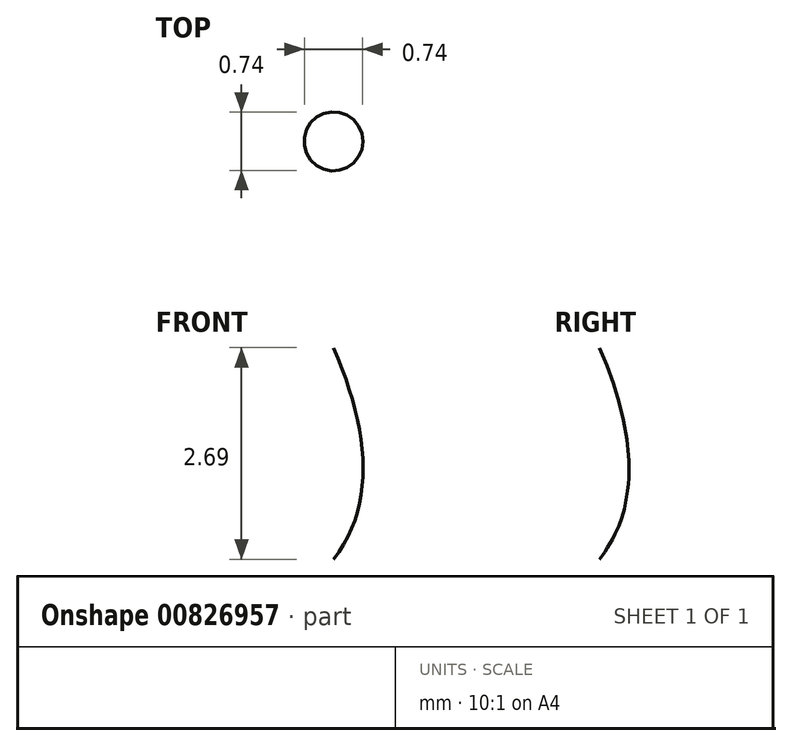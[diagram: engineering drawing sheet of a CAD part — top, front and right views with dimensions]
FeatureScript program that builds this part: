
annotation { "Feature Type Name" : "Feature", "Feature Type Description" : "" }
export const myFeature = defineFeature(function(context is Context, id is Id, definition is map)
    precondition{}
    {
        {
            var Q0;
            Q0=qCreatedBy(makeId("Front.planeOp"),FACE);
            var sketch = newSketch(context, id + "F0", { "sketchPlane" : qUnion([Q0])});
            skFitSpline(sketch, "E0", {"points": [v(0, -32.97) * mm, v(-38.8, -24.23) * mm, v(-52.04, 9.67) * mm, v(-24.5, 32.7) * mm, v(-12.31, 46.74) * mm, v(-19.2, 56.8) * mm, v(-14.43, 57.86) * mm, v(-7.55, 47.54) * mm, v(-16.55, 30.32) * mm, v(-40.39, 12.84) * mm, v(-41.45, -5.43) * mm, v(-27.94, -17.35) * mm, v(-8.34, -21.32) * mm, v(-2.78, -26.09) * mm, v(0, -32.97) * mm]});
            skLineSegment(sketch, "E1", {"start": v(0, 69.78) * mm, "end": v(0, -70.05) * mm});
            skSolve(sketch);
        }
        {
            var Q0;
            {var subQ0=sQuery(id+"F0.wireOp",EDGE,"E1");var subQ1=sQuery(id+"F0.wireOp",EDGE,"E0");var subQ2=makeQuery(id+"F0.imprint","INTERSECT",VERTEX,{"disambiguationData":[OD(0.0)],"derivedFrom":[subQ1,subQ0]});Q0=makeQuery(id+"F0.imprint","IMPRINT",FACE,{"disambiguationData":[TD([[makeQuery(id+"F0.imprint","IMPRINT",EDGE,{"disambiguationData":[TD([[subQ2,-1.0]])],"derivedFrom":subQ1}),-1.0]])]});}
            var Q1;
            Q1 = qSketchRegion(id + "F2", true);
            var Q2;
            Q2=sQuery(id+"F0.wireOp",EDGE,"E1");
            revolve(context, id + "F1", {"surfaceOperationType" : NewSurfaceOperationType.NEW, "entities" : qUnion([Q0, Q1]), "axis" : qUnion([Q2]), "revolveType" : RevolveType.FULL});
        }
        {
            var Q0;
            Q0=qCreatedBy(makeId("Right.planeOp"),FACE);
            var sketch = newSketch(context, id + "F2", { "sketchPlane" : qUnion([Q0])});
            skLineSegment(sketch, "E2", {"start": v(24.1, 32.57) * mm, "end": v(47.4, 15.05) * mm});
            skSolve(sketch);
        }
        {
            var Q0;
            Q0=sQuery(id+"F2.wireOp",VERTEX,"E2.start");
            var Q1;
            Q1=sQuery(id+"F2.wireOp",EDGE,"E2");
            cPlane(context, id + "F3", {"entities" : qUnion([Q0, Q1]), "cplaneType" : CPlaneType.CURVE_POINT, "offset" : 25.4 * mm, "oppositeDirection" : true, "width" : 152.4 * mm, "height" : 152.4 * mm});
        }
    });
